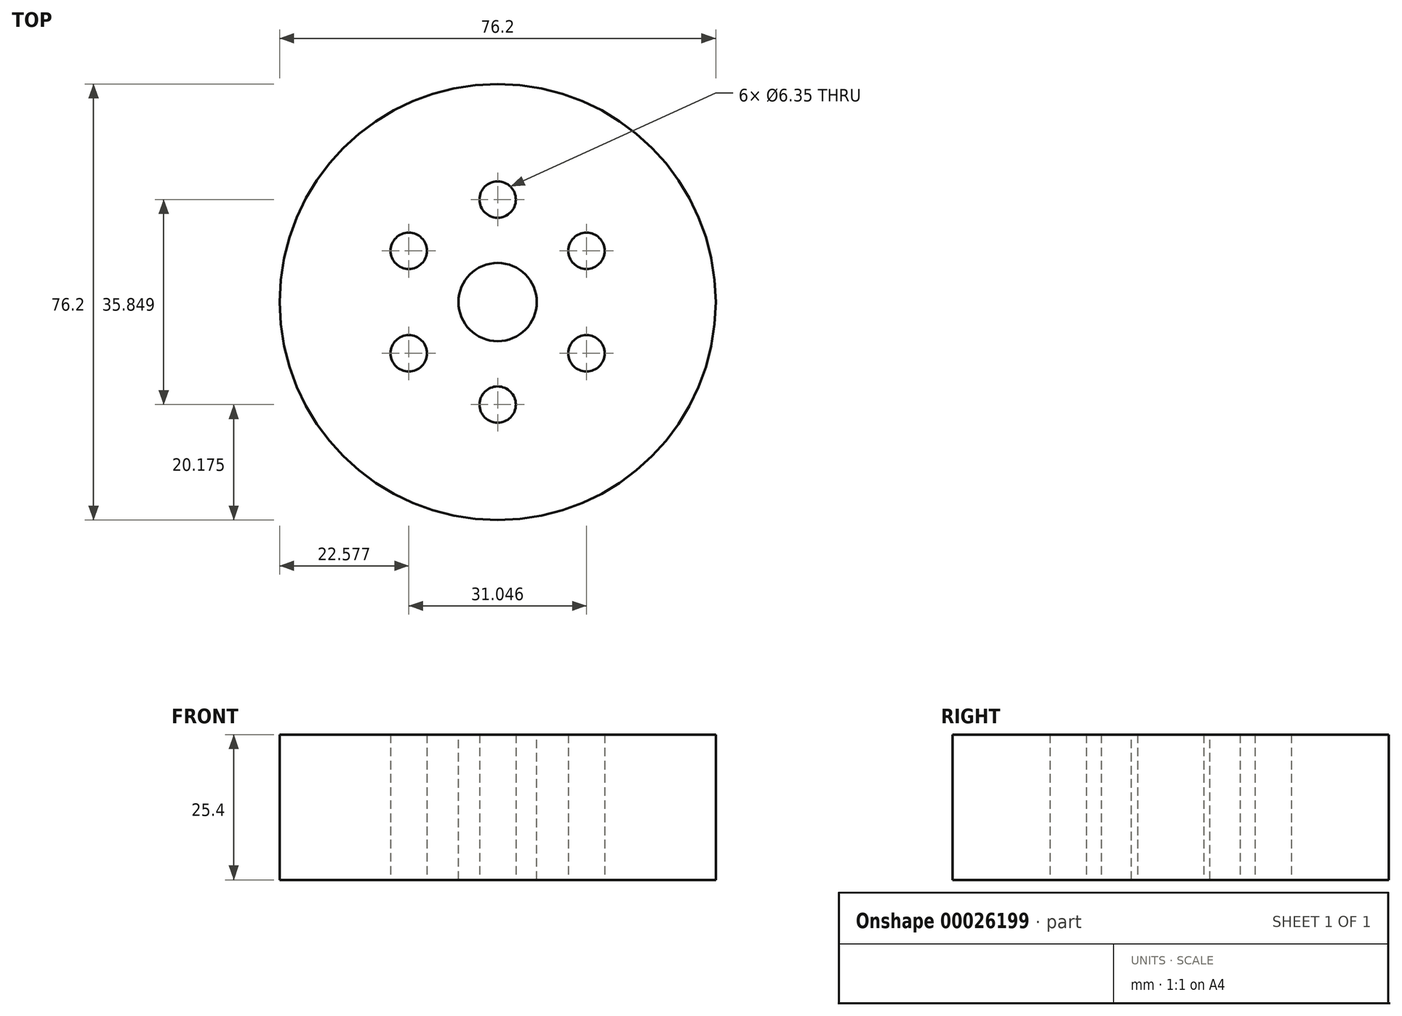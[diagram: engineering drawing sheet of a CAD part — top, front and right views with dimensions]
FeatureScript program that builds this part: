
annotation { "Feature Type Name" : "Feature", "Feature Type Description" : "" }
export const myFeature = defineFeature(function(context is Context, id is Id, definition is map)
    precondition{}
    {
        {
            var Q0;
            Q0=qCreatedBy(makeId("Top.planeOp"),FACE);
            var sketch = newSketch(context, id + "F0", { "sketchPlane" : qUnion([Q0])});
            skCircle(sketch, "E0", {"center": v(0, 0) * mm, "radius": 38.1 * mm});
            skCircle(sketch, "E1", {"center": v(0, 0) * mm, "radius": 17.92 * mm, "construction": true});
            skCircle(sketch, "E2", {"center": v(0, 17.92) * mm, "radius": 3.18 * mm});
            skCircle(sketch, "E3.1.0", {"center": v(-15.52, 8.96) * mm, "radius": 3.18 * mm});
            skCircle(sketch, "E3.2.0", {"center": v(-15.52, -8.96) * mm, "radius": 3.18 * mm});
            skCircle(sketch, "E3.3.0", {"center": v(0, -17.92) * mm, "radius": 3.18 * mm});
            skCircle(sketch, "E3.4.0", {"center": v(15.52, -8.96) * mm, "radius": 3.18 * mm});
            skCircle(sketch, "E3.5.0", {"center": v(15.52, 8.96) * mm, "radius": 3.18 * mm});
            skSolve(sketch);
        }
        {
            var Q0;
            Q0=makeQuery(id+"F0.imprint","IMPRINT",FACE,{"disambiguationData":[TD([[makeQuery(id+"F0.imprint","IMPRINT",EDGE,{"derivedFrom":sQuery(id+"F0.wireOp",EDGE,"E0")}),1.0]])]});
            extrude(context, id + "F1", {"entities" : qUnion([Q0]), "depth" : 25.4 * mm});
        }
        {
            var Q0;
            Q0=makeQuery(id+"F1.opExtrude","CAP_FACE",FACE,{"disambiguationData":[OSD([sQuery(id+"F0.wireOp",EDGE,"E0"),sQuery(id+"F0.wireOp",EDGE,"E2"),sQuery(id+"F0.wireOp",EDGE,"E3.1.0"),sQuery(id+"F0.wireOp",EDGE,"E3.2.0"),sQuery(id+"F0.wireOp",EDGE,"E3.3.0"),sQuery(id+"F0.wireOp",EDGE,"E3.4.0"),sQuery(id+"F0.wireOp",EDGE,"E3.5.0")])],"isStart":false});
            var sketch = newSketch(context, id + "F2", { "sketchPlane" : qUnion([Q0])});
            skCircle(sketch, "E4", {"center": v(0, 0) * mm, "radius": 6.84 * mm});
            skSolve(sketch);
        }
        {
            var Q0;
            Q0 = qSketchRegion(id + "F2", true);
            extrude(context, id + "F3", {"entities" : qUnion([Q0]), "operationType" : NewBodyOperationType.REMOVE, "endBound" : BoundingType.THROUGH_ALL, "oppositeDirection" : true, "depth" : 25.4 * mm});
        }
    });
